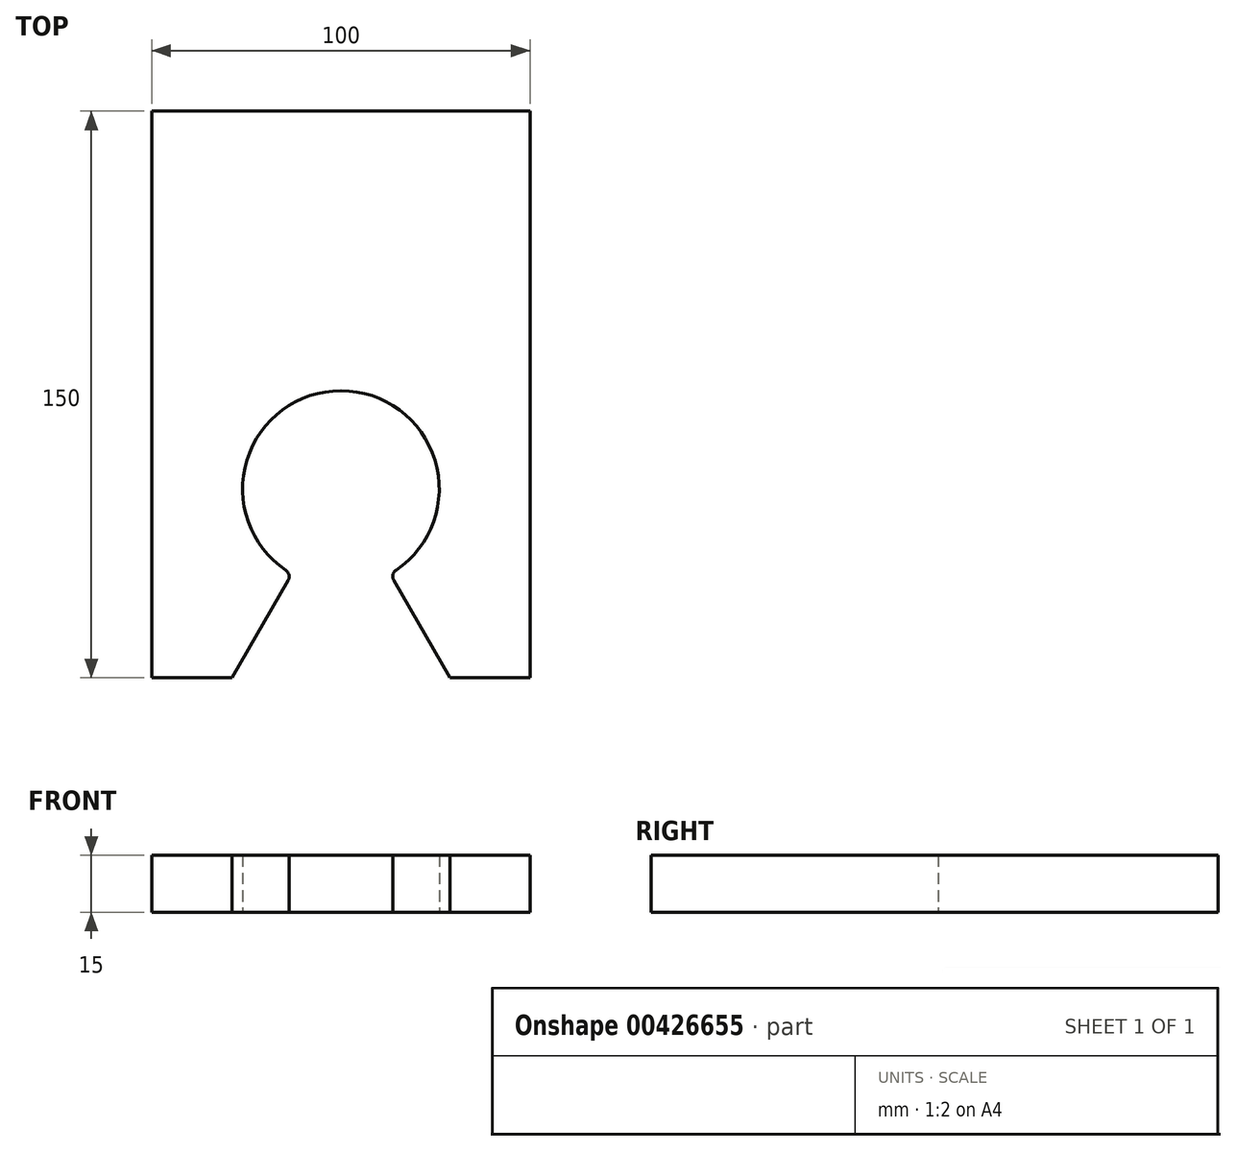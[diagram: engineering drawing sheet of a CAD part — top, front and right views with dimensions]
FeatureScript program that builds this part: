
annotation { "Feature Type Name" : "Feature", "Feature Type Description" : "" }
export const myFeature = defineFeature(function(context is Context, id is Id, definition is map)
    precondition{}
    {
        {
            var Q0;
            Q0=qCreatedBy(makeId("Top.planeOp"),FACE);
            var sketch = newSketch(context, id + "F0", { "sketchPlane" : qUnion([Q0])});
            skLineSegment(sketch, "E0.bottom", {"start": v(0, 0) * mm, "end": v(21.13, 0) * mm});
            skLineSegment(sketch, "E0.top", {"start": v(0, 150) * mm, "end": v(100, 150) * mm});
            skLineSegment(sketch, "E0.left", {"start": v(0, 0) * mm, "end": v(0, 150) * mm});
            skLineSegment(sketch, "E0.right", {"start": v(100, 0) * mm, "end": v(100, 150) * mm});
            skArc(sketch, "E1", {"start": v(64.58, 28.47) * mm, "mid": v(50, 76) * mm, "end": v(35.42, 28.47) * mm});
            skLineSegment(sketch, "E2", {"start": v(50, 150) * mm, "end": v(50, 0) * mm, "construction": true});
            skLineSegment(sketch, "E3", {"start": v(36.04, 25.81) * mm, "end": v(21.13, 0) * mm});
            skLineSegment(sketch, "E4", {"start": v(63.96, 25.81) * mm, "end": v(78.87, 0) * mm});
            skLineSegment(sketch, "E5.trimOffspring", {"start": v(78.87, 0) * mm, "end": v(100, 0) * mm});
            skPoint(sketch, "E6.visualSharp", {"position": v(37, 27.48) * mm});
            skArc(sketch, "E6.filletArc", {"start": v(36.04, 25.81) * mm, "mid": v(36.25, 27.26) * mm, "end": v(35.42, 28.47) * mm});
            skPoint(sketch, "E7.visualSharp", {"position": v(63, 27.48) * mm});
            skArc(sketch, "E7.filletArc", {"start": v(64.58, 28.47) * mm, "mid": v(63.75, 27.26) * mm, "end": v(63.96, 25.81) * mm});
            skSolve(sketch);
        }
        {
            var Q0;
            Q0 = qSketchRegion(id + "F0", true);
            extrude(context, id + "F1", {"entities" : qUnion([Q0]), "depth" : 15 * mm});
        }
    });
